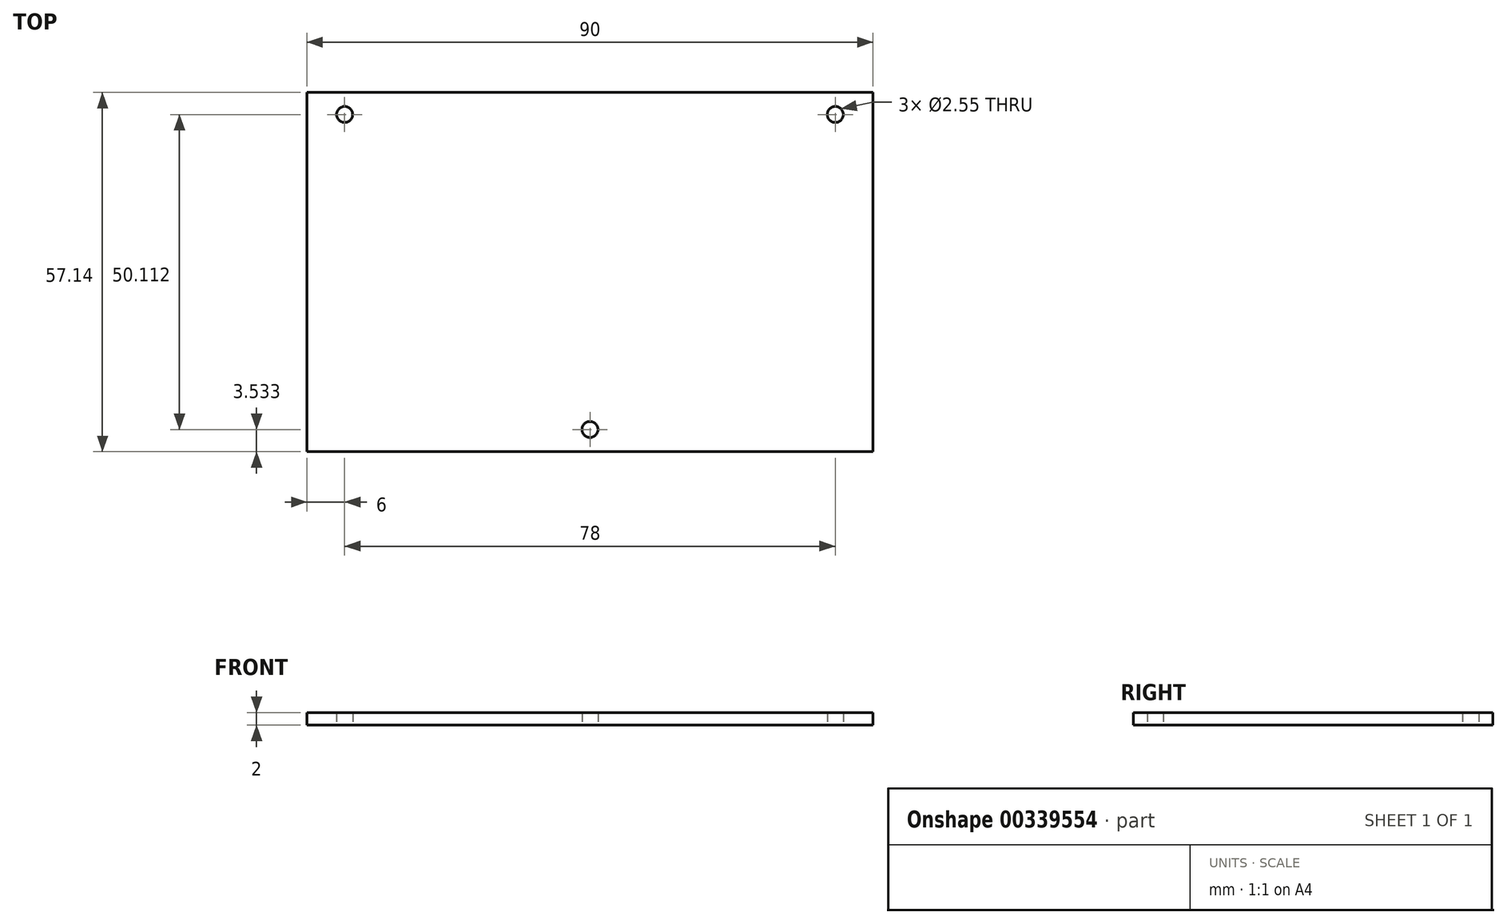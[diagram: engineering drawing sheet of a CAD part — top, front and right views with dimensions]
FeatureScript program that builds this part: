
annotation { "Feature Type Name" : "Feature", "Feature Type Description" : "" }
export const myFeature = defineFeature(function(context is Context, id is Id, definition is map)
    precondition{}
    {
        {
            var Q0;
            Q0=qCreatedBy(makeId("Top.planeOp"),FACE);
            var sketch = newSketch(context, id + "F0", { "sketchPlane" : qUnion([Q0])});
            skLineSegment(sketch, "E0.bottom", {"start": v(-45, 28.58) * mm, "end": v(0, 28.58) * mm});
            skLineSegment(sketch, "E0.top", {"start": v(-45, -28.58) * mm, "end": v(0, -28.58) * mm});
            skLineSegment(sketch, "E0.left", {"start": v(-45, 28.58) * mm, "end": v(-45, -28.57) * mm});
            skPoint(sketch, "E0.middle", {"position": v(0, 0) * mm});
            skCircle(sketch, "E1", {"center": v(-39, 25.08) * mm, "radius": 1.27 * mm});
            skArc(sketch, "E2", {"start": v(0, -23.76) * mm, "mid": v(-1.27, -25.04) * mm, "end": v(0, -26.31) * mm});
            skLineSegment(sketch, "E3", {"start": v(0, 28.58) * mm, "end": v(0, -28.58) * mm});
            skPoint(sketch, "E4.orphan", {"position": v(45, 28.58) * mm});
            skPoint(sketch, "E5.orphan", {"position": v(45, -28.58) * mm});
            skCircle(sketch, "E6.0", {"center": v(-39, 25.08) * mm, "radius": 2.77 * mm});
            skArc(sketch, "E7.0", {"start": v(0, -22.26) * mm, "mid": v(-2.77, -25.04) * mm, "end": v(0, -27.81) * mm});
            skSolve(sketch);
        }
        {
            var Q0;
            {var subQ2=sQuery(id+"F0.wireOp",EDGE,"E0.bottom");Q0=makeQuery(id+"F0.imprint","IMPRINT",FACE,{"disambiguationData":[TD([[makeQuery(id+"F0.imprint","IMPRINT",EDGE,{"derivedFrom":subQ2}),-1.0]])]});}
            var Q1;
            {var subQ0=sQuery(id+"F0.wireOp",EDGE,"E2");Q1=makeQuery(id+"F0.imprint","IMPRINT",FACE,{"disambiguationData":[TD([[makeQuery(id+"F0.imprint","IMPRINT",EDGE,{"derivedFrom":subQ0}),-1.0]])]});}
            var Q2;
            Q2=makeQuery(id+"F0.imprint","IMPRINT",FACE,{"disambiguationData":[TD([[makeQuery(id+"F0.imprint","IMPRINT",EDGE,{"derivedFrom":sQuery(id+"F0.wireOp",EDGE,"E1")}),-1.0]])]});
            extrude(context, id + "F1", {"entities" : qUnion([Q0, Q1, Q2]), "depth" : 2 * mm});
        }
        {
            var Q0;
            Q0=makeQuery(id+"F1.opExtrude","SWEPT_BODY",BODY,{"disambiguationData":[OSD([sQuery(id+"F0.wireOp",EDGE,"E0.bottom"),sQuery(id+"F0.wireOp",EDGE,"E0.top"),sQuery(id+"F0.wireOp",EDGE,"E0.left"),sQuery(id+"F0.wireOp",EDGE,"E1"),sQuery(id+"F0.wireOp",EDGE,"E2"),sQuery(id+"F0.wireOp",EDGE,"E3")])]});
            var Q1;
            {var subQ0=sQuery(id+"F0.wireOp",EDGE,"E3");Q1=makeQuery(id+"F1.opExtrude","SWEPT_FACE",FACE,{"disambiguationData":[OSD([subQ0]),TDD([makeQuery(id+"F0.imprint","IMPRINT",EDGE,{"disambiguationData":[TD([[makeQuery(id+"F0.imprint","INTERSECT",VERTEX,{"derivedFrom":[sQuery(id+"F0.wireOp",EDGE,"E0.bottom"),subQ0]}),-1.0]])],"derivedFrom":subQ0}),makeQuery(id+"F0.imprint","IMPRINT",EDGE,{"disambiguationData":[TD([[makeQuery(id+"F0.imprint","INTERSECT",VERTEX,{"disambiguationData":[OD(0.0)],"derivedFrom":[sQuery(id+"F0.wireOp",EDGE,"E2"),subQ0]}),1.0]])],"derivedFrom":subQ0})])]});}
            mirror(context, id + "F2", {"operationType" : NewBodyOperationType.ADD, "entities" : qUnion([Q0]), "mirrorPlane" : qUnion([Q1])});
        }
    });
